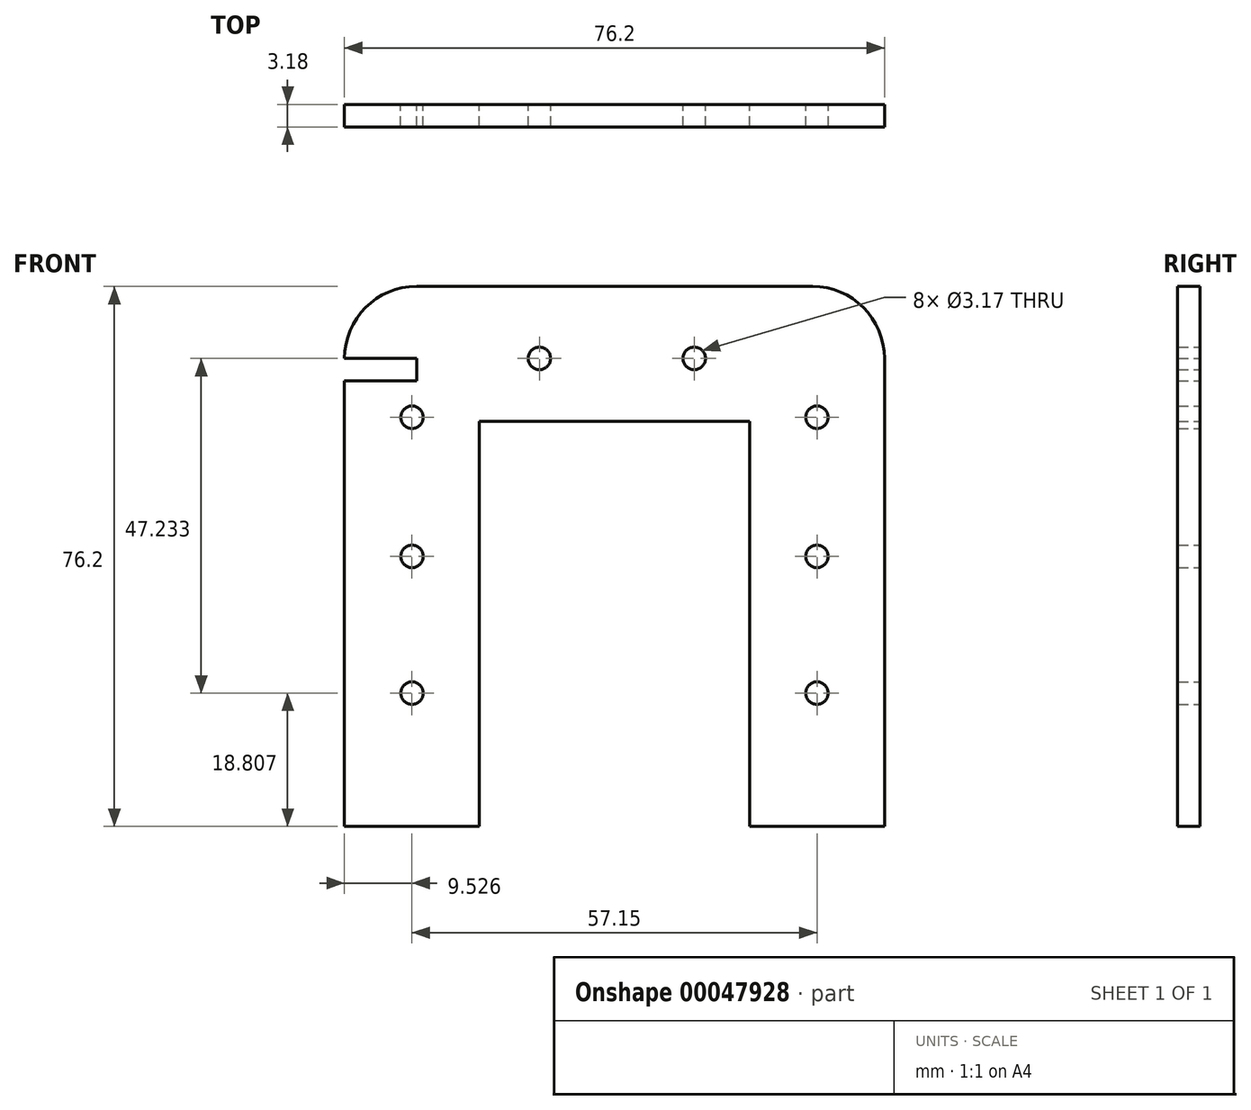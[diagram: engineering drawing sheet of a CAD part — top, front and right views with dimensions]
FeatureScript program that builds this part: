
annotation { "Feature Type Name" : "Feature", "Feature Type Description" : "" }
export const myFeature = defineFeature(function(context is Context, id is Id, definition is map)
    precondition{}
    {
        {
            var Q0;
            Q0=qCreatedBy(makeId("Front.planeOp"),FACE);
            var sketch = newSketch(context, id + "F0", { "sketchPlane" : qUnion([Q0])});
            skLineSegment(sketch, "E0.bottom", {"start": v(-60.86, -31.18) * mm, "end": v(-41.8, -31.18) * mm});
            skLineSegment(sketch, "E0.top", {"start": v(-60.86, 45.02) * mm, "end": v(-51.97, 45.02) * mm});
            skLineSegment(sketch, "E0.left", {"start": v(-60.86, -31.18) * mm, "end": v(-60.86, 25.97) * mm});
            skLineSegment(sketch, "E0.right", {"start": v(-41.8, -31.18) * mm, "end": v(-41.8, 34.86) * mm});
            skLineSegment(sketch, "E1.bottom", {"start": v(-60.86, 45.02) * mm, "end": v(-107.85, 45.02) * mm});
            skLineSegment(sketch, "E1.top", {"start": v(-60.86, 25.97) * mm, "end": v(-98.96, 25.97) * mm});
            skLineSegment(sketch, "E1.right", {"start": v(-118, 31.68) * mm, "end": v(-118, 25.97) * mm});
            skLineSegment(sketch, "E2.top", {"start": v(-118, -31.18) * mm, "end": v(-98.96, -31.18) * mm});
            skLineSegment(sketch, "E2.left", {"start": v(-118, 25.97) * mm, "end": v(-118, -31.18) * mm});
            skLineSegment(sketch, "E2.right", {"start": v(-98.96, 25.97) * mm, "end": v(-98.96, -31.18) * mm});
            skCircle(sketch, "E3", {"center": v(-108.48, 26.55) * mm, "radius": 1.59 * mm});
            skCircle(sketch, "E4", {"center": v(-108.48, 6.92) * mm, "radius": 1.59 * mm});
            skCircle(sketch, "E5", {"center": v(-108.48, -12.37) * mm, "radius": 1.59 * mm});
            skCircle(sketch, "E6", {"center": v(-51.33, 26.55) * mm, "radius": 1.59 * mm});
            skCircle(sketch, "E7", {"center": v(-51.33, 6.92) * mm, "radius": 1.59 * mm});
            skCircle(sketch, "E8", {"center": v(-51.33, -12.37) * mm, "radius": 1.59 * mm});
            skPoint(sketch, "E9.startSnap0", {"position": v(-90.51, 34.86) * mm});
            skCircle(sketch, "E10", {"center": v(-90.51, 34.86) * mm, "radius": 1.59 * mm});
            skPoint(sketch, "E11.visualSharp", {"position": v(-118, 45.02) * mm});
            skArc(sketch, "E11.filletArc", {"start": v(-107.85, 45.02) * mm, "mid": v(-115.03, 42.04) * mm, "end": v(-118, 34.86) * mm});
            skPoint(sketch, "E12.visualSharp", {"position": v(-41.8, 45.02) * mm});
            skArc(sketch, "E12.filletArc", {"start": v(-41.8, 34.86) * mm, "mid": v(-44.78, 42.04) * mm, "end": v(-51.97, 45.02) * mm});
            skCircle(sketch, "E13", {"center": v(-68.66, 34.86) * mm, "radius": 1.59 * mm});
            skLineSegment(sketch, "E14.bottom", {"start": v(-118, 31.68) * mm, "end": v(-107.85, 31.68) * mm});
            skLineSegment(sketch, "E14.top", {"start": v(-118, 34.86) * mm, "end": v(-107.85, 34.86) * mm});
            skLineSegment(sketch, "E14.right", {"start": v(-107.85, 31.68) * mm, "end": v(-107.85, 34.86) * mm});
            skSolve(sketch);
        }
        {
            var Q0;
            Q0=makeQuery(id+"F0.imprint","IMPRINT",FACE,{"disambiguationData":[TD([[makeQuery(id+"F0.imprint","IMPRINT",EDGE,{"derivedFrom":sQuery(id+"F0.wireOp",EDGE,"E0.bottom")}),1.0]])]});
            extrude(context, id + "F1", {"entities" : qUnion([Q0]), "depth" : 3.17 * mm});
        }
    });
